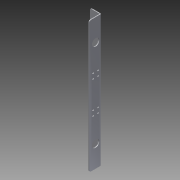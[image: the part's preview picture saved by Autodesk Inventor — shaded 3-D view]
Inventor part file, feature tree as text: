
AUTODESK INVENTOR PART (.ipt)
format: ipt  version: 2014 SP1 (Build 180222100, 222)  size: 317,952 bytes
history: native  units: in
note: dims shown in document units (in); Inventor stores cm internally (conversion verified against a paired STEP export)
features: other x5, sketch x4, reference x4, sheet_metal_op x2, chamfer x2, plane x1
ambient origin geometry x8: Origin, YZ Plane, XZ Plane, XY Plane, X Axis, Y Axis, Z Axis, Center Point
bodies: Solid1 (feature_tree)
feature tree (18):
  sketch  "Sketch1"  dims[d0=3.1914in]
  sheet_metal_op  "Face1"
  sheet_metal_op  "Fold1"
  plane  "Work Plane1"
  chamfer  "Corner Round1"
  chamfer  "Corner Round2"
  other  "Plate1"
  sketch  "Sketch2"  dims[d1=20.0in]
  sketch  "Sketch3"  dims[d2=1.75in]
  sketch  "Sketch4"  dims[d3=0.01in d4=0.25in d5=0.25in d6=11.811in d8=0.6638in d9=0.3937in d11=1.0in d13=0.125in d14=0.125in d15=0.0625in d16=0.25in d17=0.125in d18=90.0deg d19=0.05in d20=1.125in d21=0.875in d22=13.35in d23=0.125in d24=0.0in d26=0.266in d27=0.5in d31=0.55in d33=0.25in d34=0.75in d35=0.266in d38=1.05in d44=13.35in d46=0.125in d47=0.0in d51=0.55in d52=0.25in d54=0.266in d55=0.266in d57=0.75in d58=0.266in d60=0.266in d62=0.125in d63=0.0in d64=0.375in d69=0.75in d70=0.375in d71=0.25in d72=0.55in d73=0.7874in d75=1.05in d76=0.7874in d78=0.75in d81=0.35in d82=0.875in d83=0.875in d84=5.0in d85=3.1496in d87=1.4286in d88=0.3937in d90=1.0in]
  reference  "Reference3"
  reference  "Reference4"
  reference  "Reference5"
  reference  "Reference6"
  other  "Cut1"
  other  "Cut2"
  other  "Cut3"
  other  "Definition1"
